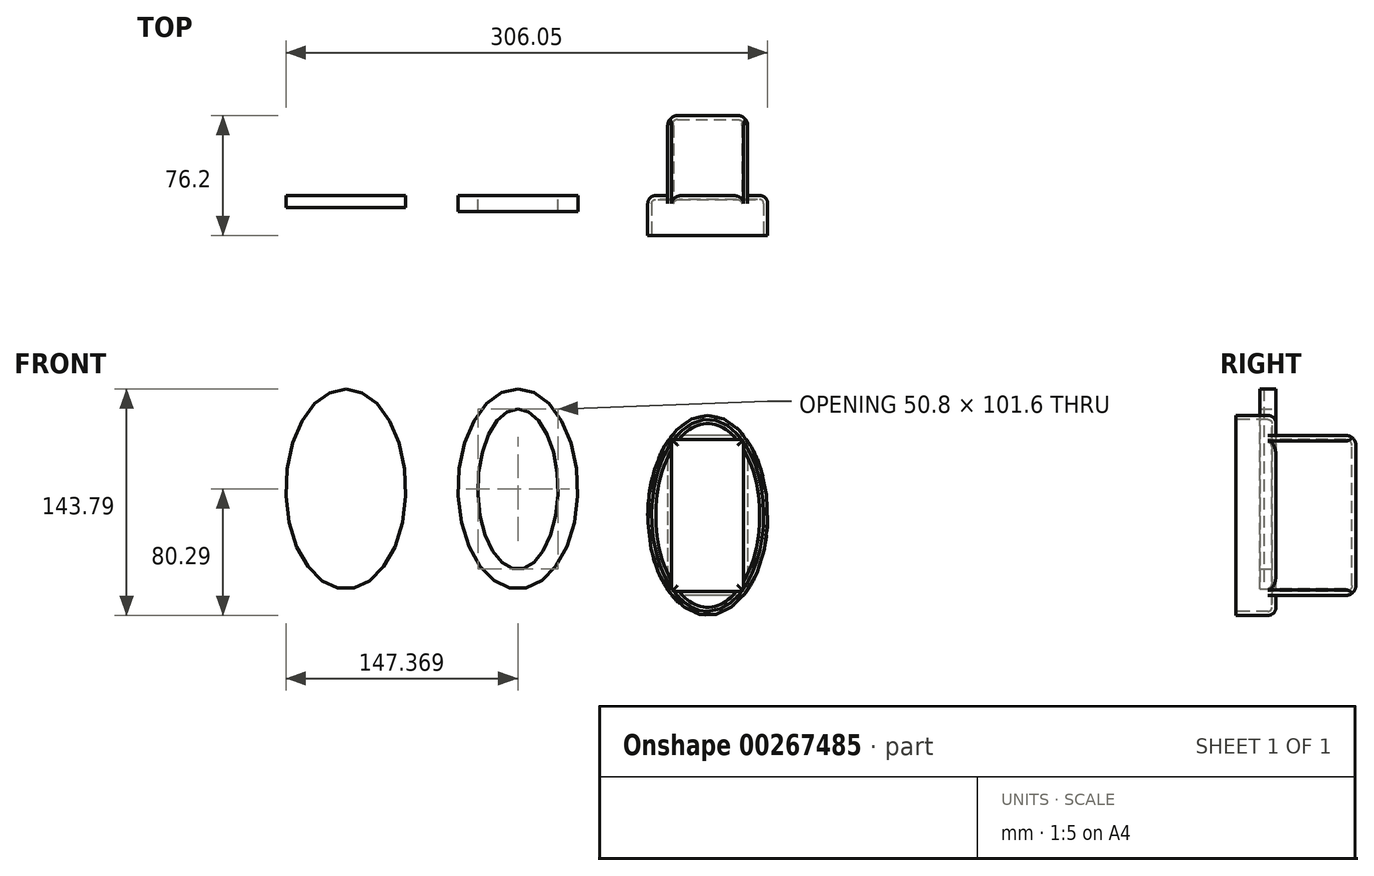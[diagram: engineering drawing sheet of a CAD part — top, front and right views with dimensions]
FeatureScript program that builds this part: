
annotation { "Feature Type Name" : "Feature", "Feature Type Description" : "" }
export const myFeature = defineFeature(function(context is Context, id is Id, definition is map)
    precondition{}
    {
        {
            var Q0;
            Q0=qCreatedBy(makeId("Front.planeOp"),FACE);
            var sketch = newSketch(context, id + "F0", { "sketchPlane" : qUnion([Q0])});
            skLineSegment(sketch, "E0.bottom", {"start": v(25.4, 50.8) * mm, "end": v(-25.4, 50.8) * mm});
            skLineSegment(sketch, "E0.top", {"start": v(25.4, -50.8) * mm, "end": v(-25.4, -50.8) * mm});
            skLineSegment(sketch, "E0.left", {"start": v(25.4, 50.8) * mm, "end": v(25.4, -50.8) * mm});
            skLineSegment(sketch, "E0.right", {"start": v(-25.4, 50.8) * mm, "end": v(-25.4, -50.8) * mm});
            skPoint(sketch, "E0.middle", {"position": v(0, 0) * mm});
            skEllipse(sketch, "E1", {"center": v(0, 0) * mm, "majorRadius": 63.5 * mm, "minorRadius": 38.1 * mm, "majorAxis": v(0, 1)});
            skEllipse(sketch, "E2", {"center": v(-120.58, 16.79) * mm, "majorRadius": 63.5 * mm, "minorRadius": 38.1 * mm, "majorAxis": v(0, 1)});
            skEllipse(sketch, "E3", {"center": v(-120.58, 16.79) * mm, "majorRadius": 50.8 * mm, "minorRadius": 25.4 * mm, "majorAxis": v(0, 1)});
            skEllipse(sketch, "E4", {"center": v(-229.85, 16.71) * mm, "majorRadius": 63.5 * mm, "minorRadius": 38.1 * mm, "majorAxis": v(0, 1)});
            skSolve(sketch);
        }
        {
            var Q0;
            {var subQ0=sQuery(id+"F0.wireOp",EDGE,"E1");var subQ9=sQuery(id+"F0.wireOp",EDGE,"E0.bottom");var subQ10=makeQuery(id+"F0.imprint","INTERSECT",VERTEX,{"disambiguationData":[OD(0.0)],"derivedFrom":[subQ9,subQ0]});Q0=makeQuery(id+"F0.imprint","IMPRINT",FACE,{"disambiguationData":[TD([[makeQuery(id+"F0.imprint","IMPRINT",EDGE,{"disambiguationData":[TD([[subQ10,-1.0]])],"derivedFrom":subQ9}),1.0]])]});}
            extrude(context, id + "F1", {"entities" : qUnion([Q0]), "oppositeDirection" : true, "depth" : 50.8 * mm});
        }
        {
            var Q0;
            Q0=makeQuery(id+"F1.opExtrude","CAP_EDGE",EDGE,{"disambiguationData":[OSD([sQuery(id+"F0.wireOp",EDGE,"E0.top")])],"isStart":false});
            var Q1;
            Q1=makeQuery(id+"F1.opExtrude","CAP_EDGE",EDGE,{"disambiguationData":[OSD([sQuery(id+"F0.wireOp",EDGE,"E0.right")])],"isStart":false});
            var Q2;
            Q2=makeQuery(id+"F1.opExtrude","CAP_EDGE",EDGE,{"disambiguationData":[OSD([sQuery(id+"F0.wireOp",EDGE,"E0.left")])],"isStart":false});
            var Q3;
            Q3=makeQuery(id+"F1.opExtrude","CAP_EDGE",EDGE,{"disambiguationData":[OSD([sQuery(id+"F0.wireOp",EDGE,"E0.bottom")])],"isStart":false});
            var Q4;
            {var subQ0=sQuery(id+"F0.wireOp",EDGE,"E1");Q4=makeQuery(id+"F1.opExtrude","CAP_EDGE",EDGE,{"disambiguationData":[OSD([subQ0]),TDD([makeQuery(id+"F0.imprint","IMPRINT",EDGE,{"disambiguationData":[TD([[makeQuery(id+"F0.imprint","INTERSECT",VERTEX,{"disambiguationData":[OD(0.0)],"derivedFrom":[sQuery(id+"F0.wireOp",EDGE,"E0.top"),subQ0]}),-1.0]])],"derivedFrom":subQ0})])],"isStart":false});}
            var Q5;
            {var subQ0=sQuery(id+"F0.wireOp",EDGE,"E1");Q5=makeQuery(id+"F1.opExtrude","CAP_EDGE",EDGE,{"disambiguationData":[OSD([subQ0]),TDD([makeQuery(id+"F0.imprint","IMPRINT",EDGE,{"disambiguationData":[TD([[makeQuery(id+"F0.imprint","INTERSECT",VERTEX,{"disambiguationData":[OD(1.0)],"derivedFrom":[sQuery(id+"F0.wireOp",EDGE,"E0.top"),subQ0]}),1.0]])],"derivedFrom":subQ0})])],"isStart":false});}
            var Q6;
            {var subQ0=sQuery(id+"F0.wireOp",EDGE,"E1");Q6=makeQuery(id+"F1.opExtrude","CAP_EDGE",EDGE,{"disambiguationData":[OSD([subQ0]),TDD([makeQuery(id+"F0.imprint","IMPRINT",EDGE,{"disambiguationData":[TD([[makeQuery(id+"F0.imprint","INTERSECT",VERTEX,{"disambiguationData":[OD(1.0)],"derivedFrom":[sQuery(id+"F0.wireOp",EDGE,"E0.bottom"),subQ0]}),-1.0]])],"derivedFrom":subQ0})])],"isStart":false});}
            var Q7;
            {var subQ0=sQuery(id+"F0.wireOp",EDGE,"E1");Q7=makeQuery(id+"F1.opExtrude","CAP_EDGE",EDGE,{"disambiguationData":[OSD([subQ0]),TDD([makeQuery(id+"F0.imprint","IMPRINT",EDGE,{"disambiguationData":[TD([[makeQuery(id+"F0.imprint","INTERSECT",VERTEX,{"disambiguationData":[OD(0.0)],"derivedFrom":[sQuery(id+"F0.wireOp",EDGE,"E0.bottom"),subQ0]}),1.0]])],"derivedFrom":subQ0})])],"isStart":false});}
            fillet(context, id + "F2", {"entities" : qUnion([Q0, Q1, Q2, Q3, Q4, Q5, Q6, Q7]), "radius" : 6.35 * mm, "tangentPropagation" : true, "allowEdgeOverflow" : false});
        }
        {
            var Q0;
            {var subQ0=sQuery(id+"F0.wireOp",EDGE,"E1");var subQ1=sQuery(id+"F0.wireOp",EDGE,"E0.right");var subQ2=makeQuery(id+"F0.imprint","INTERSECT",VERTEX,{"disambiguationData":[OD(0.0)],"derivedFrom":[subQ1,subQ0]});Q0=makeQuery(id+"F0.imprint","IMPRINT",FACE,{"disambiguationData":[TD([[makeQuery(id+"F0.imprint","IMPRINT",EDGE,{"disambiguationData":[TD([[subQ2,-1.0]])],"derivedFrom":subQ1}),-1.0]])]});}
            var Q1;
            {var subQ0=sQuery(id+"F0.wireOp",EDGE,"E1");var subQ9=sQuery(id+"F0.wireOp",EDGE,"E0.bottom");var subQ10=makeQuery(id+"F0.imprint","INTERSECT",VERTEX,{"disambiguationData":[OD(0.0)],"derivedFrom":[subQ9,subQ0]});Q1=makeQuery(id+"F0.imprint","IMPRINT",FACE,{"disambiguationData":[TD([[makeQuery(id+"F0.imprint","IMPRINT",EDGE,{"disambiguationData":[TD([[subQ10,-1.0]])],"derivedFrom":subQ9}),1.0]])]});}
            var Q2;
            {var subQ0=sQuery(id+"F0.wireOp",EDGE,"E1");var subQ1=sQuery(id+"F0.wireOp",EDGE,"E0.top");var subQ2=makeQuery(id+"F0.imprint","INTERSECT",VERTEX,{"disambiguationData":[OD(0.0)],"derivedFrom":[subQ1,subQ0]});Q2=makeQuery(id+"F0.imprint","IMPRINT",FACE,{"disambiguationData":[TD([[makeQuery(id+"F0.imprint","IMPRINT",EDGE,{"disambiguationData":[TD([[subQ2,-1.0]])],"derivedFrom":subQ1}),1.0]])]});}
            var Q3;
            {var subQ0=sQuery(id+"F0.wireOp",EDGE,"E1");var subQ1=sQuery(id+"F0.wireOp",EDGE,"E0.left");var subQ2=makeQuery(id+"F0.imprint","INTERSECT",VERTEX,{"disambiguationData":[OD(0.0)],"derivedFrom":[subQ1,subQ0]});Q3=makeQuery(id+"F0.imprint","IMPRINT",FACE,{"disambiguationData":[TD([[makeQuery(id+"F0.imprint","IMPRINT",EDGE,{"disambiguationData":[TD([[subQ2,-1.0]])],"derivedFrom":subQ1}),1.0]])]});}
            var Q4;
            {var subQ0=sQuery(id+"F0.wireOp",EDGE,"E1");var subQ1=sQuery(id+"F0.wireOp",EDGE,"E0.bottom");var subQ2=makeQuery(id+"F0.imprint","INTERSECT",VERTEX,{"disambiguationData":[OD(0.0)],"derivedFrom":[subQ1,subQ0]});Q4=makeQuery(id+"F0.imprint","IMPRINT",FACE,{"disambiguationData":[TD([[makeQuery(id+"F0.imprint","IMPRINT",EDGE,{"disambiguationData":[TD([[subQ2,-1.0]])],"derivedFrom":subQ1}),-1.0]])]});}
            extrude(context, id + "F3", {"entities" : qUnion([Q0, Q1, Q2, Q3, Q4]), "operationType" : NewBodyOperationType.ADD, "depth" : 25.4 * mm});
        }
        {
            var Q0;
            {var subQ0=sQuery(id+"F0.wireOp",EDGE,"E1");var subQ1=sQuery(id+"F0.wireOp",EDGE,"E0.top");Q0=makeQuery(id+"F3.boolean.opBoolean","SPLIT",EDGE,{"disambiguationData":[TD([makeQuery(id+"F1.opExtrude","SWEPT_FACE",FACE,{"disambiguationData":[OSD([subQ1])]})])],"derivedFrom":makeQuery(id+"F3.opExtrude","CAP_EDGE",EDGE,{"disambiguationData":[OSD([subQ0])],"isStart":true})});}
            var Q1;
            {var subQ0=sQuery(id+"F0.wireOp",EDGE,"E1");var subQ2=sQuery(id+"F0.wireOp",EDGE,"E0.left");Q1=makeQuery(id+"F3.boolean.opBoolean","SPLIT",EDGE,{"disambiguationData":[TD([makeQuery(id+"F1.opExtrude","SWEPT_FACE",FACE,{"disambiguationData":[OSD([subQ2])]})])],"derivedFrom":makeQuery(id+"F3.opExtrude","CAP_EDGE",EDGE,{"disambiguationData":[OSD([subQ0])],"isStart":true})});}
            var Q2;
            {var subQ0=sQuery(id+"F0.wireOp",EDGE,"E1");var subQ3=sQuery(id+"F0.wireOp",EDGE,"E0.right");Q2=makeQuery(id+"F3.boolean.opBoolean","SPLIT",EDGE,{"disambiguationData":[TD([makeQuery(id+"F1.opExtrude","SWEPT_FACE",FACE,{"disambiguationData":[OSD([subQ3])]})])],"derivedFrom":makeQuery(id+"F3.opExtrude","CAP_EDGE",EDGE,{"disambiguationData":[OSD([subQ0])],"isStart":true})});}
            var Q3;
            {var subQ0=sQuery(id+"F0.wireOp",EDGE,"E1");var subQ4=sQuery(id+"F0.wireOp",EDGE,"E0.bottom");Q3=makeQuery(id+"F3.boolean.opBoolean","SPLIT",EDGE,{"disambiguationData":[TD([makeQuery(id+"F1.opExtrude","SWEPT_FACE",FACE,{"disambiguationData":[OSD([subQ4])]})])],"derivedFrom":makeQuery(id+"F3.opExtrude","CAP_EDGE",EDGE,{"disambiguationData":[OSD([subQ0])],"isStart":true})});}
            fillet(context, id + "F4", {"entities" : qUnion([Q0, Q1, Q2, Q3]), "radius" : 5.08 * mm, "tangentPropagation" : true, "allowEdgeOverflow" : false});
        }
        {
            var Q0;
            Q0=makeQuery(id+"F3.opExtrude","CAP_FACE",FACE,{"disambiguationData":[OSD([sQuery(id+"F0.wireOp",EDGE,"E1")])],"isStart":false});
            shell(context, id + "F5", {"entities" : qUnion([Q0]), "thickness" : 2.54 * mm});
        }
        {
            var Q0;
            Q0=makeQuery(id+"F0.imprint","IMPRINT",FACE,{"disambiguationData":[TD([[makeQuery(id+"F0.imprint","IMPRINT",EDGE,{"derivedFrom":sQuery(id+"F0.wireOp",EDGE,"E2")}),1.0]])]});
            extrude(context, id + "F6", {"entities" : qUnion([Q0]), "depth" : 10.16 * mm});
        }
        {
            var Q0;
            Q0=makeQuery(id+"F0.imprint","IMPRINT",FACE,{"disambiguationData":[TD([[makeQuery(id+"F0.imprint","IMPRINT",EDGE,{"derivedFrom":sQuery(id+"F0.wireOp",EDGE,"E4")}),1.0]])]});
            extrude(context, id + "F7", {"entities" : qUnion([Q0]), "depth" : 7.62 * mm});
        }
    });
